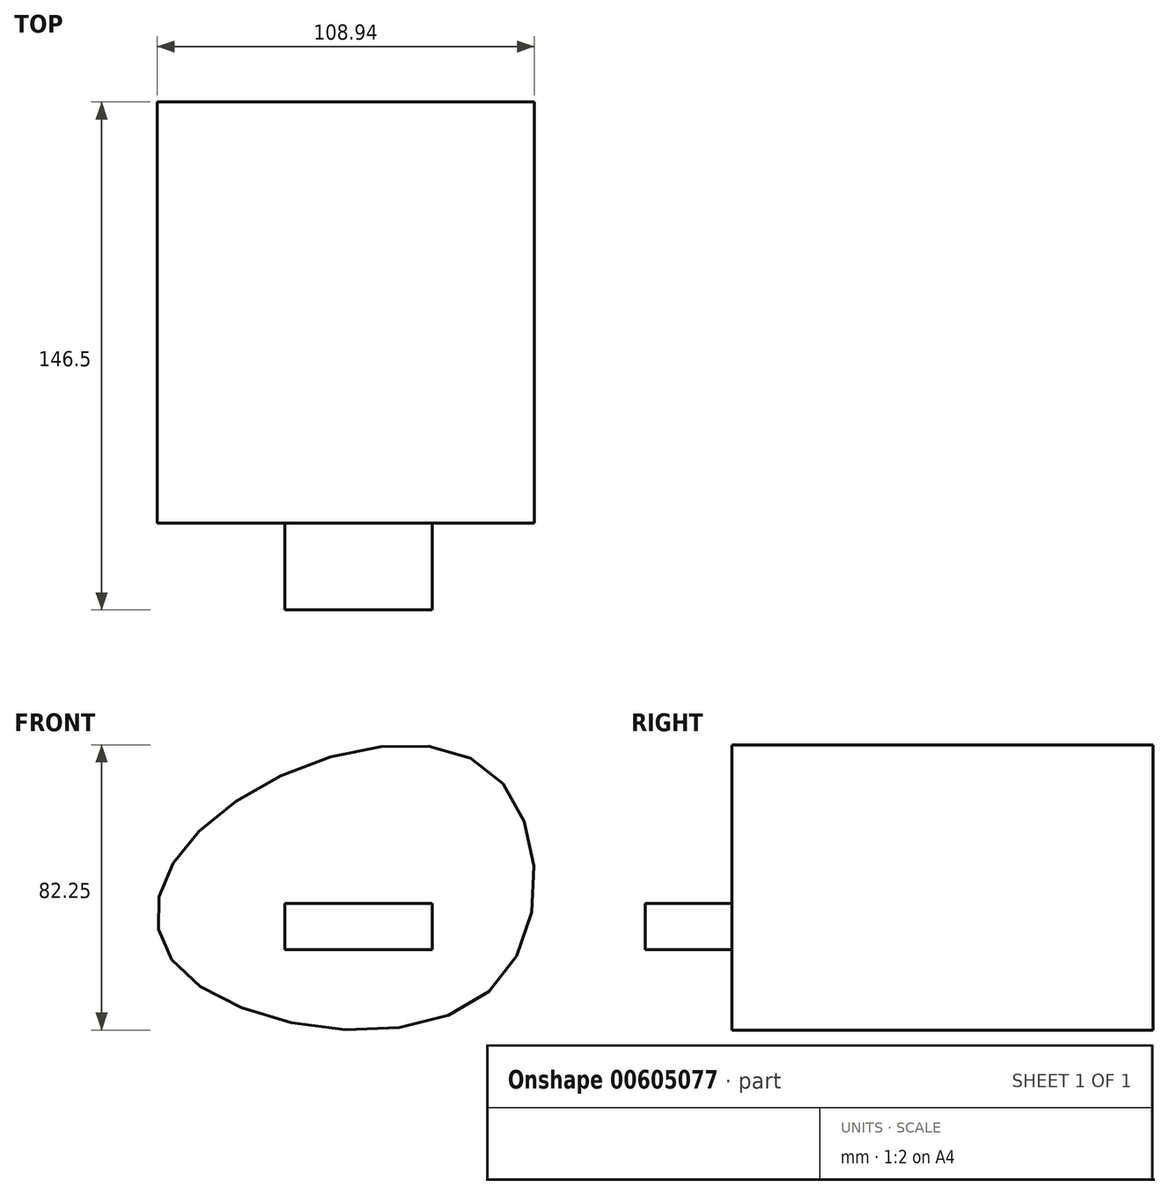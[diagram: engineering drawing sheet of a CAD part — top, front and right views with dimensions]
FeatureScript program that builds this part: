
annotation { "Feature Type Name" : "Feature", "Feature Type Description" : "" }
export const myFeature = defineFeature(function(context is Context, id is Id, definition is map)
    precondition{}
    {
        {
            var Q0;
            Q0=qCreatedBy(makeId("Front.planeOp"),FACE);
            var sketch = newSketch(context, id + "F0", { "sketchPlane" : qUnion([Q0])});
            skFitSpline(sketch, "E0", {"points": [v(-56.8, 46.24) * mm, v(25.64, 64.85) * mm, v(26.94, 0) * mm, v(-61.34, 5.34) * mm, v(-56.8, 46.24) * mm]});
            skSolve(sketch);
        }
        {
            var Q0;
            Q0=makeQuery(id+"F0.imprint","IMPRINT",FACE,{"disambiguationData":[TD([[makeQuery(id+"F0.imprint","IMPRINT",EDGE,{"derivedFrom":sQuery(id+"F0.wireOp",EDGE,"E0")}),-1.0]])]});
            extrude(context, id + "F1", {"entities" : qUnion([Q0]), "depth" : 25 * mm, "offsetDistance" : 25 * mm});
        }
        {
            var Q0;
            Q0=makeQuery(id+"F1.opExtrude","CAP_FACE",FACE,{"disambiguationData":[OSD([sQuery(id+"F0.wireOp",EDGE,"E0")])],"isStart":false});
            extrude(context, id + "F2", {"entities" : qUnion([Q0]), "operationType" : NewBodyOperationType.ADD, "depth" : 96.5 * mm, "offsetDistance" : 25 * mm});
        }
        {
            var Q0;
            Q0=makeQuery(id+"F2.opExtrude","CAP_FACE",FACE,{"disambiguationData":[OSD([sQuery(id+"F0.wireOp",EDGE,"E0")])],"isStart":false});
            var sketch = newSketch(context, id + "F3", { "sketchPlane" : qUnion([Q0])});
            skLineSegment(sketch, "E1.bottom", {"start": v(-32.05, 25.36) * mm, "end": v(10.59, 25.36) * mm});
            skLineSegment(sketch, "E1.top", {"start": v(-32.05, 12.06) * mm, "end": v(10.59, 12.06) * mm});
            skLineSegment(sketch, "E1.left", {"start": v(-32.05, 25.36) * mm, "end": v(-32.05, 12.06) * mm});
            skLineSegment(sketch, "E1.right", {"start": v(10.59, 25.36) * mm, "end": v(10.59, 12.06) * mm});
            skSolve(sketch);
        }
        {
            var Q0;
            Q0=makeQuery(id+"F3.imprint","IMPRINT",FACE,{"disambiguationData":[TD([[makeQuery(id+"F3.imprint","IMPRINT",EDGE,{"derivedFrom":sQuery(id+"F3.wireOp",EDGE,"E1.bottom")}),-1.0]])]});
            extrude(context, id + "F4", {"entities" : qUnion([Q0]), "operationType" : NewBodyOperationType.ADD, "depth" : 25 * mm, "offsetDistance" : 25 * mm});
        }
    });
